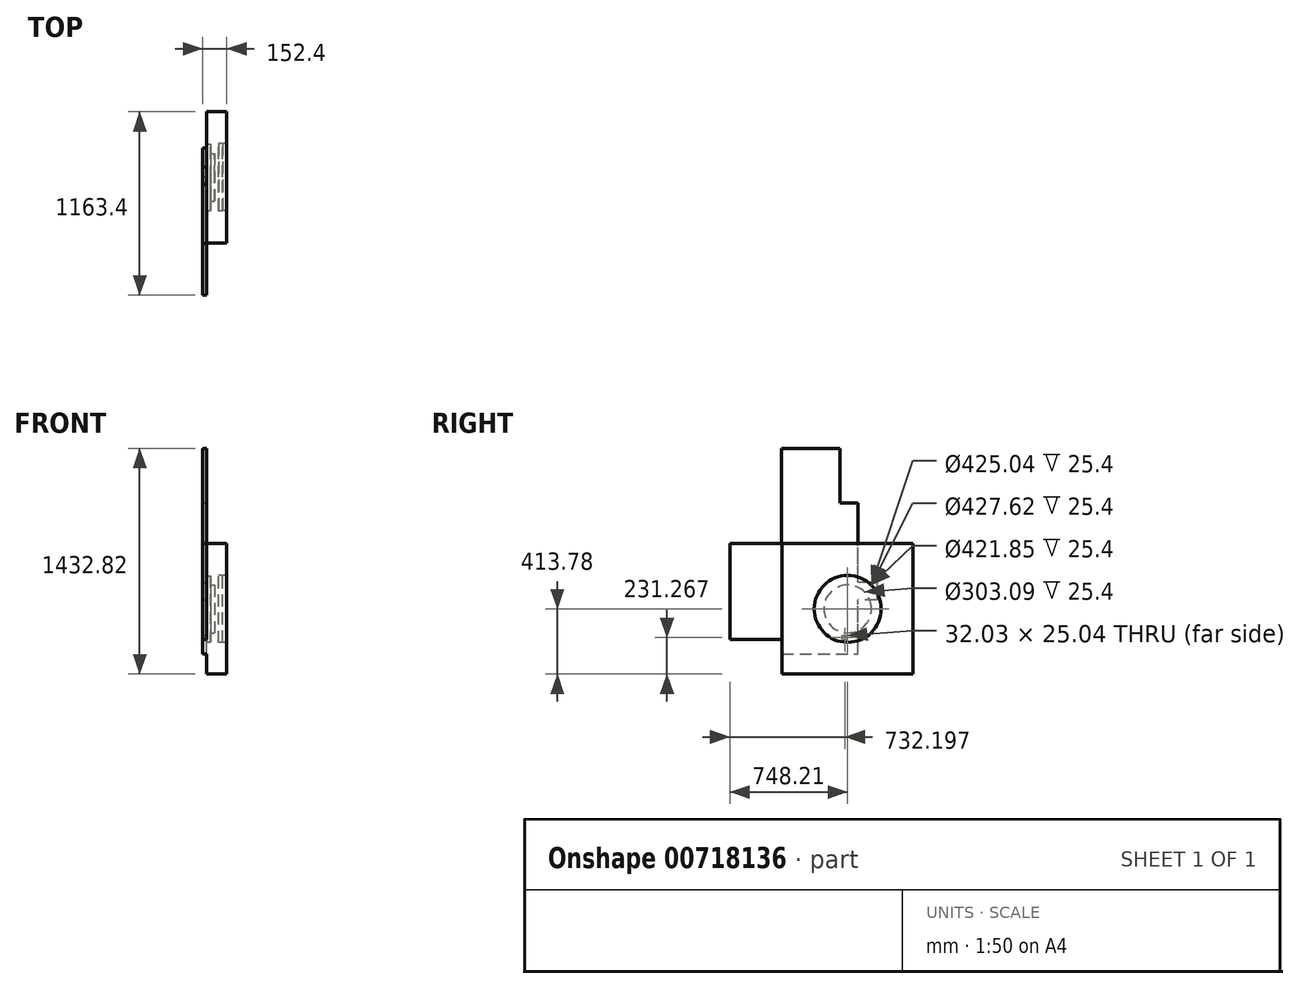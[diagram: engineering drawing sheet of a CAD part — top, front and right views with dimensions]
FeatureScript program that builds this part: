
annotation { "Feature Type Name" : "Feature", "Feature Type Description" : "" }
export const myFeature = defineFeature(function(context is Context, id is Id, definition is map)
    precondition{}
    {
        {
            var Q0;
            Q0=qCreatedBy(makeId("Right.planeOp"),FACE);
            var sketch = newSketch(context, id + "F0", { "sketchPlane" : qUnion([Q0])});
            skLineSegment(sketch, "E0.bottom", {"start": v(-598.19, 196.12) * mm, "end": v(-1588.91, 196.12) * mm});
            skLineSegment(sketch, "E0.top", {"start": v(-598.19, 401.9) * mm, "end": v(-1588.91, 401.9) * mm});
            skLineSegment(sketch, "E0.left", {"start": v(-598.19, 196.12) * mm, "end": v(-598.19, 401.9) * mm});
            skLineSegment(sketch, "E0.right", {"start": v(-1588.91, 196.12) * mm, "end": v(-1588.91, 401.9) * mm});
            skLineSegment(sketch, "E1.bottom", {"start": v(-598.19, 196.12) * mm, "end": v(-1197.36, 196.12) * mm});
            skLineSegment(sketch, "E1.top", {"start": v(-598.19, 145.68) * mm, "end": v(-1197.36, 145.68) * mm});
            skLineSegment(sketch, "E1.left", {"start": v(-598.19, 196.12) * mm, "end": v(-598.19, 145.68) * mm});
            skLineSegment(sketch, "E1.right", {"start": v(-1197.36, 196.12) * mm, "end": v(-1197.36, 145.68) * mm});
            skLineSegment(sketch, "E2.bottom", {"start": v(-598.19, 145.68) * mm, "end": v(-833.03, 145.68) * mm});
            skLineSegment(sketch, "E2.top", {"start": v(-598.19, 78.2) * mm, "end": v(-833.03, 78.2) * mm});
            skLineSegment(sketch, "E2.left", {"start": v(-598.19, 145.68) * mm, "end": v(-598.19, 78.2) * mm});
            skLineSegment(sketch, "E2.right", {"start": v(-833.03, 145.68) * mm, "end": v(-833.03, 78.2) * mm});
            skLineSegment(sketch, "E3.bottom", {"start": v(-598.19, 183.7) * mm, "end": v(698.48, 183.7) * mm});
            skLineSegment(sketch, "E3.top", {"start": v(-598.19, 8.74) * mm, "end": v(698.48, 8.74) * mm});
            skLineSegment(sketch, "E3.left", {"start": v(-598.19, 183.7) * mm, "end": v(-598.19, 8.74) * mm});
            skLineSegment(sketch, "E3.right", {"start": v(698.48, 183.7) * mm, "end": v(698.48, 8.74) * mm});
            skLineSegment(sketch, "E4.bottom", {"start": v(-605.86, 78.2) * mm, "end": v(-1548.13, 78.2) * mm});
            skLineSegment(sketch, "E4.top", {"start": v(-605.86, 215.32) * mm, "end": v(-1548.13, 215.32) * mm});
            skLineSegment(sketch, "E4.left", {"start": v(-605.86, 78.2) * mm, "end": v(-605.86, 215.32) * mm});
            skLineSegment(sketch, "E4.right", {"start": v(-1548.13, 78.2) * mm, "end": v(-1548.13, 215.32) * mm});
            skLineSegment(sketch, "E5.bottom", {"start": v(-605.86, 215.32) * mm, "end": v(-1588.91, 215.32) * mm});
            skLineSegment(sketch, "E5.top", {"start": v(-605.86, 401.9) * mm, "end": v(-1588.91, 401.9) * mm});
            skLineSegment(sketch, "E5.left", {"start": v(-605.86, 215.32) * mm, "end": v(-605.86, 401.9) * mm});
            skLineSegment(sketch, "E5.right", {"start": v(-1588.91, 215.32) * mm, "end": v(-1588.91, 401.9) * mm});
            skSolve(sketch);
        }
        {
            var Q0;
            Q0 = qSketchRegion(id + "F0", true);
            extrude(context, id + "F1", {"entities" : qUnion([Q0]), "depth" : 25.4 * mm, "offsetDistance" : 25.4 * mm});
        }
        {
            var Q0;
            Q0=makeQuery(id+"F1.opExtrude","CAP_FACE",FACE,{"disambiguationData":[OSD([sQuery(id+"F0.wireOp",EDGE,"E0.bottom"),sQuery(id+"F0.wireOp",EDGE,"E0.top"),sQuery(id+"F0.wireOp",EDGE,"E0.left"),sQuery(id+"F0.wireOp",EDGE,"E0.right"),sQuery(id+"F0.wireOp",EDGE,"E1.bottom"),sQuery(id+"F0.wireOp",EDGE,"E1.top"),sQuery(id+"F0.wireOp",EDGE,"E1.left"),sQuery(id+"F0.wireOp",EDGE,"E1.right"),sQuery(id+"F0.wireOp",EDGE,"E2.bottom"),sQuery(id+"F0.wireOp",EDGE,"E2.top"),sQuery(id+"F0.wireOp",EDGE,"E3.bottom"),sQuery(id+"F0.wireOp",EDGE,"E3.top"),sQuery(id+"F0.wireOp",EDGE,"E3.left"),sQuery(id+"F0.wireOp",EDGE,"E3.right"),sQuery(id+"F0.wireOp",EDGE,"E4.bottom"),sQuery(id+"F0.wireOp",EDGE,"E4.left"),sQuery(id+"F0.wireOp",EDGE,"E4.right"),sQuery(id+"F0.wireOp",EDGE,"E5.top"),sQuery(id+"F0.wireOp",EDGE,"E5.right")])],"isStart":true});
            var sketch = newSketch(context, id + "F2", { "sketchPlane" : qUnion([Q0])});
            skLineSegment(sketch, "E6.bottom", {"start": v(805.67, 562.42) * mm, "end": v(91.89, 562.42) * mm});
            skLineSegment(sketch, "E6.top", {"start": v(805.67, -160.03) * mm, "end": v(91.89, -160.03) * mm});
            skLineSegment(sketch, "E6.left", {"start": v(805.67, 562.42) * mm, "end": v(805.67, -160.03) * mm});
            skLineSegment(sketch, "E6.right", {"start": v(91.89, 562.42) * mm, "end": v(91.89, -160.03) * mm});
            skSolve(sketch);
        }
        {
            var Q0;
            Q0 = qSketchRegion(id + "F2", true);
            extrude(context, id + "F3", {"entities" : qUnion([Q0]), "operationType" : NewBodyOperationType.ADD, "depth" : 10751.3 * mm, "offsetDistance" : 25.4 * mm});
        }
        {
            var Q0;
            Q0=makeQuery(id+"F1.opExtrude","SWEPT_BODY",BODY,{"disambiguationData":[OSD([sQuery(id+"F0.wireOp",EDGE,"E0.bottom"),sQuery(id+"F0.wireOp",EDGE,"E0.top"),sQuery(id+"F0.wireOp",EDGE,"E0.left"),sQuery(id+"F0.wireOp",EDGE,"E0.right"),sQuery(id+"F0.wireOp",EDGE,"E1.bottom"),sQuery(id+"F0.wireOp",EDGE,"E1.top"),sQuery(id+"F0.wireOp",EDGE,"E1.left"),sQuery(id+"F0.wireOp",EDGE,"E1.right"),sQuery(id+"F0.wireOp",EDGE,"E2.bottom"),sQuery(id+"F0.wireOp",EDGE,"E2.top"),sQuery(id+"F0.wireOp",EDGE,"E3.bottom"),sQuery(id+"F0.wireOp",EDGE,"E3.top"),sQuery(id+"F0.wireOp",EDGE,"E3.left"),sQuery(id+"F0.wireOp",EDGE,"E3.right"),sQuery(id+"F0.wireOp",EDGE,"E4.bottom"),sQuery(id+"F0.wireOp",EDGE,"E4.left"),sQuery(id+"F0.wireOp",EDGE,"E4.right"),sQuery(id+"F0.wireOp",EDGE,"E5.top"),sQuery(id+"F0.wireOp",EDGE,"E5.right")])]});
            deleteBodies(context, id + "F4", {"entities" : qUnion([Q0])});
        }
        {
            var Q0;
            Q0=qCreatedBy(makeId("Right.planeOp"),FACE);
            var sketch = newSketch(context, id + "F5", { "sketchPlane" : qUnion([Q0])});
            skLineSegment(sketch, "E7.bottom", {"start": v(415.2, -413.78) * mm, "end": v(-418.49, -413.78) * mm});
            skLineSegment(sketch, "E7.top", {"start": v(415.2, 415.13) * mm, "end": v(-418.49, 415.13) * mm});
            skLineSegment(sketch, "E7.left", {"start": v(415.2, -413.78) * mm, "end": v(415.2, 415.13) * mm});
            skLineSegment(sketch, "E7.right", {"start": v(-418.49, -413.78) * mm, "end": v(-418.49, 415.13) * mm});
            skSolve(sketch);
        }
        {
            var Q0;
            Q0 = qSketchRegion(id + "F5", true);
            extrude(context, id + "F6", {"entities" : qUnion([Q0]), "depth" : 25.4 * mm, "offsetDistance" : 25.4 * mm});
        }
        {
            var Q0;
            Q0=makeQuery(id+"F6.opExtrude","CAP_FACE",FACE,{"disambiguationData":[OSD([sQuery(id+"F5.wireOp",EDGE,"E7.bottom"),sQuery(id+"F5.wireOp",EDGE,"E7.top"),sQuery(id+"F5.wireOp",EDGE,"E7.left"),sQuery(id+"F5.wireOp",EDGE,"E7.right")])],"isStart":false});
            var sketch = newSketch(context, id + "F7", { "sketchPlane" : qUnion([Q0])});
            skCircle(sketch, "E8", {"center": v(0, 0) * mm, "radius": 213.81 * mm});
            skLineSegment(sketch, "E9.bottom", {"start": v(-418.49, 415.13) * mm, "end": v(415.2, 415.13) * mm});
            skLineSegment(sketch, "E9.top", {"start": v(-418.49, -413.78) * mm, "end": v(415.2, -413.78) * mm});
            skLineSegment(sketch, "E9.left", {"start": v(-418.49, 415.13) * mm, "end": v(-418.49, -413.78) * mm});
            skLineSegment(sketch, "E9.right", {"start": v(415.2, 415.13) * mm, "end": v(415.2, -413.78) * mm});
            skSolve(sketch);
        }
        {
            var Q0;
            Q0 = qSketchRegion(id + "F7", true);
            extrude(context, id + "F8", {"entities" : qUnion([Q0]), "operationType" : NewBodyOperationType.ADD, "depth" : 25.4 * mm, "offsetDistance" : 25.4 * mm});
        }
        {
            var Q0;
            Q0=makeQuery(id+"F8.opExtrude","CAP_FACE",FACE,{"disambiguationData":[OSD([sQuery(id+"F7.wireOp",EDGE,"E8"),sQuery(id+"F7.wireOp",EDGE,"E9.bottom"),sQuery(id+"F7.wireOp",EDGE,"E9.top"),sQuery(id+"F7.wireOp",EDGE,"E9.left"),sQuery(id+"F7.wireOp",EDGE,"E9.right")])],"isStart":false});
            var sketch = newSketch(context, id + "F9", { "sketchPlane" : qUnion([Q0])});
            skCircle(sketch, "E10", {"center": v(0, 0) * mm, "radius": 212.52 * mm});
            skLineSegment(sketch, "E11.bottom", {"start": v(-418.49, 415.13) * mm, "end": v(387.19, 415.13) * mm});
            skLineSegment(sketch, "E11.top", {"start": v(-418.49, -413.78) * mm, "end": v(387.19, -413.78) * mm});
            skLineSegment(sketch, "E11.left", {"start": v(-418.49, 415.13) * mm, "end": v(-418.49, -413.78) * mm});
            skLineSegment(sketch, "E11.right", {"start": v(387.19, 415.13) * mm, "end": v(387.19, -413.78) * mm});
            skLineSegment(sketch, "E12.bottom", {"start": v(415.2, 415.13) * mm, "end": v(387.19, 415.13) * mm});
            skLineSegment(sketch, "E12.top", {"start": v(415.2, -413.78) * mm, "end": v(387.19, -413.78) * mm});
            skLineSegment(sketch, "E12.left", {"start": v(415.2, 415.13) * mm, "end": v(415.2, -413.78) * mm});
            skSolve(sketch);
        }
        {
            var Q0;
            Q0 = qSketchRegion(id + "F9", true);
            extrude(context, id + "F10", {"entities" : qUnion([Q0]), "operationType" : NewBodyOperationType.ADD, "depth" : 25.4 * mm, "offsetDistance" : 25.4 * mm});
        }
        {
            var Q0;
            Q0=makeQuery(id+"F6.opExtrude","CAP_FACE",FACE,{"disambiguationData":[OSD([sQuery(id+"F5.wireOp",EDGE,"E7.bottom"),sQuery(id+"F5.wireOp",EDGE,"E7.top"),sQuery(id+"F5.wireOp",EDGE,"E7.left"),sQuery(id+"F5.wireOp",EDGE,"E7.right")])],"isStart":true});
            var sketch = newSketch(context, id + "F11", { "sketchPlane" : qUnion([Q0])});
            skLineSegment(sketch, "E13.bottom", {"start": v(-415.2, 415.13) * mm, "end": v(418.49, 415.13) * mm});
            skLineSegment(sketch, "E13.top", {"start": v(-415.2, -413.78) * mm, "end": v(418.49, -413.78) * mm});
            skLineSegment(sketch, "E13.left", {"start": v(-415.2, 415.13) * mm, "end": v(-415.2, -413.78) * mm});
            skLineSegment(sketch, "E13.right", {"start": v(418.49, 415.13) * mm, "end": v(418.49, -413.78) * mm});
            skCircle(sketch, "E14", {"center": v(0, 0) * mm, "radius": 151.55 * mm});
            skSolve(sketch);
        }
        {
            var Q0;
            Q0 = qSketchRegion(id + "F11", true);
            extrude(context, id + "F12", {"entities" : qUnion([Q0]), "operationType" : NewBodyOperationType.ADD, "depth" : 25.4 * mm, "offsetDistance" : 25.4 * mm});
        }
        {
            var Q0;
            Q0=makeQuery(id+"F12.opExtrude","CAP_FACE",FACE,{"disambiguationData":[OSD([sQuery(id+"F11.wireOp",EDGE,"E13.bottom"),sQuery(id+"F11.wireOp",EDGE,"E13.top"),sQuery(id+"F11.wireOp",EDGE,"E13.left"),sQuery(id+"F11.wireOp",EDGE,"E13.right"),sQuery(id+"F11.wireOp",EDGE,"E14")])],"isStart":false});
            var sketch = newSketch(context, id + "F13", { "sketchPlane" : qUnion([Q0])});
            skCircle(sketch, "E15", {"center": v(0, 0) * mm, "radius": 210.93 * mm});
            skLineSegment(sketch, "E16.bottom", {"start": v(-415.2, -413.78) * mm, "end": v(265.24, -413.78) * mm});
            skLineSegment(sketch, "E16.top", {"start": v(-415.2, 254) * mm, "end": v(265.24, 254) * mm});
            skLineSegment(sketch, "E16.left", {"start": v(-415.2, -413.78) * mm, "end": v(-415.2, 254) * mm});
            skLineSegment(sketch, "E16.right", {"start": v(265.24, -413.78) * mm, "end": v(265.24, 254) * mm});
            skSolve(sketch);
        }
        {
            var Q0;
            Q0 = qSketchRegion(id + "F13", true);
            extrude(context, id + "F14", {"entities" : qUnion([Q0]), "operationType" : NewBodyOperationType.ADD, "depth" : 25.4 * mm, "offsetDistance" : 25.4 * mm});
        }
        {
            var Q0;
            {var subQ0=sQuery(id+"F11.wireOp",EDGE,"E13.top");var subQ1=sQuery(id+"F11.wireOp",EDGE,"E13.bottom");var subQ2=sQuery(id+"F11.wireOp",EDGE,"E13.left");var subQ3=sQuery(id+"F11.wireOp",EDGE,"E13.right");Q0=makeQuery(id+"F14.boolean.opBoolean","SPLIT",FACE,{"disambiguationData":[TD([makeQuery(id+"F6.opExtrude","SWEPT_FACE",FACE,{"disambiguationData":[OSD([sQuery(id+"F5.wireOp",EDGE,"E7.bottom")])]})])],"derivedFrom":makeQuery(id+"F12.opExtrude","CAP_FACE",FACE,{"disambiguationData":[OSD([subQ1,subQ0,subQ2,subQ3,sQuery(id+"F11.wireOp",EDGE,"E14")])],"isStart":false})});}
            var sketch = newSketch(context, id + "F15", { "sketchPlane" : qUnion([Q0])});
            skPoint(sketch, "E17.oppositeSnap0", {"position": v(-74.98, 254) * mm});
            skLineSegment(sketch, "E17.bottom", {"start": v(-415.2, 415.13) * mm, "end": v(418.49, 415.13) * mm});
            skLineSegment(sketch, "E17.top", {"start": v(-415.2, 254) * mm, "end": v(418.49, 254) * mm});
            skLineSegment(sketch, "E17.left", {"start": v(-415.2, 415.13) * mm, "end": v(-415.2, 254) * mm});
            skLineSegment(sketch, "E17.right", {"start": v(418.49, 415.13) * mm, "end": v(418.49, 254) * mm});
            skLineSegment(sketch, "E18.bottom", {"start": v(418.49, 254) * mm, "end": v(265.24, 254) * mm});
            skLineSegment(sketch, "E18.top", {"start": v(418.49, -413.78) * mm, "end": v(265.24, -413.78) * mm});
            skLineSegment(sketch, "E18.left", {"start": v(418.49, 254) * mm, "end": v(418.49, -413.78) * mm});
            skLineSegment(sketch, "E18.right", {"start": v(265.24, 254) * mm, "end": v(265.24, -413.78) * mm});
            skSolve(sketch);
        }
        {
            var Q0;
            Q0 = qSketchRegion(id + "F15", true);
            extrude(context, id + "F16", {"entities" : qUnion([Q0]), "operationType" : NewBodyOperationType.ADD, "depth" : 25.4 * mm, "offsetDistance" : 25.4 * mm});
        }
        {
            var Q0;
            Q0=makeQuery(id+"F16.boolean.opBoolean","MERGE",FACE,{"derivedFrom":[makeQuery(id+"F14.opExtrude","CAP_FACE",FACE,{"disambiguationData":[OSD([sQuery(id+"F13.wireOp",EDGE,"E15"),sQuery(id+"F13.wireOp",EDGE,"E16.bottom"),sQuery(id+"F13.wireOp",EDGE,"E16.top"),sQuery(id+"F13.wireOp",EDGE,"E16.left"),sQuery(id+"F13.wireOp",EDGE,"E16.right")])],"isStart":false}),makeQuery(id+"F16.opExtrude","CAP_FACE",FACE,{"disambiguationData":[OSD([sQuery(id+"F15.wireOp",EDGE,"E17.bottom"),sQuery(id+"F15.wireOp",EDGE,"E17.top"),sQuery(id+"F15.wireOp",EDGE,"E17.left"),sQuery(id+"F15.wireOp",EDGE,"E17.right"),sQuery(id+"F15.wireOp",EDGE,"E18.top"),sQuery(id+"F15.wireOp",EDGE,"E18.left"),sQuery(id+"F15.wireOp",EDGE,"E18.right")])],"isStart":false})]});
            var sketch = newSketch(context, id + "F17", { "sketchPlane" : qUnion([Q0])});
            skLineSegment(sketch, "E19.bottom", {"start": v(47.38, 415.13) * mm, "end": v(421.76, 415.13) * mm});
            skLineSegment(sketch, "E19.top", {"start": v(47.38, 1019.04) * mm, "end": v(421.76, 1019.04) * mm});
            skLineSegment(sketch, "E19.left", {"start": v(47.38, 415.13) * mm, "end": v(47.38, 1019.04) * mm});
            skLineSegment(sketch, "E19.right", {"start": v(421.76, 415.13) * mm, "end": v(421.76, 1019.04) * mm});
            skLineSegment(sketch, "E20.bottom", {"start": v(418.49, 415.13) * mm, "end": v(748.2, 415.13) * mm});
            skLineSegment(sketch, "E20.top", {"start": v(418.49, -194.47) * mm, "end": v(748.2, -194.47) * mm});
            skLineSegment(sketch, "E20.left", {"start": v(418.49, 415.13) * mm, "end": v(418.49, -194.47) * mm});
            skLineSegment(sketch, "E20.right", {"start": v(748.2, 415.13) * mm, "end": v(748.2, -194.47) * mm});
            skLineSegment(sketch, "E21.bottom", {"start": v(418.49, -220.99) * mm, "end": v(418.49, -220.99) * mm});
            skLineSegment(sketch, "E21.top", {"start": v(418.49, 0.68) * mm, "end": v(418.49, 0.68) * mm});
            skLineSegment(sketch, "E21.left", {"start": v(418.49, -220.99) * mm, "end": v(418.49, 0.68) * mm});
            skLineSegment(sketch, "E21.right", {"start": v(418.49, -220.99) * mm, "end": v(418.49, 0.68) * mm});
            skLineSegment(sketch, "E22.bottom", {"start": v(32.03, -195.03) * mm, "end": v(0, -195.03) * mm});
            skLineSegment(sketch, "E22.top", {"start": v(32.03, -170) * mm, "end": v(0, -170) * mm});
            skLineSegment(sketch, "E22.left", {"start": v(32.03, -195.03) * mm, "end": v(32.03, -170) * mm});
            skLineSegment(sketch, "E22.right", {"start": v(0, -195.03) * mm, "end": v(0, -170) * mm});
            skLineSegment(sketch, "E23.bottom", {"start": v(418.49, -285.76) * mm, "end": v(-65.54, -285.76) * mm});
            skLineSegment(sketch, "E23.top", {"start": v(418.49, 671.52) * mm, "end": v(-65.54, 671.52) * mm});
            skLineSegment(sketch, "E23.left", {"start": v(418.49, -285.76) * mm, "end": v(418.49, 671.52) * mm});
            skLineSegment(sketch, "E23.right", {"start": v(-65.54, -285.76) * mm, "end": v(-65.54, 671.52) * mm});
            skLineSegment(sketch, "E24.bottom", {"start": v(-184.9, 168.35) * mm, "end": v(-65.54, 168.35) * mm});
            skLineSegment(sketch, "E24.top", {"start": v(-184.9, 57.17) * mm, "end": v(-65.54, 57.17) * mm});
            skLineSegment(sketch, "E24.left", {"start": v(-184.9, 168.35) * mm, "end": v(-184.9, 57.17) * mm});
            skLineSegment(sketch, "E24.right", {"start": v(-65.54, 168.35) * mm, "end": v(-65.54, 57.17) * mm});
            skSolve(sketch);
        }
        {
            var Q0;
            Q0 = qSketchRegion(id + "F17", true);
            extrude(context, id + "F18", {"entities" : qUnion([Q0]), "operationType" : NewBodyOperationType.ADD, "depth" : 25.4 * mm, "offsetDistance" : 25.4 * mm});
        }
    });
